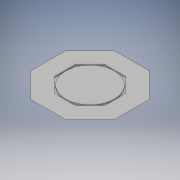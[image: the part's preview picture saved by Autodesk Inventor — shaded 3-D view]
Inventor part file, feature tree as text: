
AUTODESK INVENTOR PART (.ipt)
format: ipt  version: 2016 SP2 (Build 200236200, 236)  size: 265,216 bytes
history: native  units: mm
features: sketch x5, extrude x3, sweep x1, projected_geometry x1
ambient origin geometry x8: Origin, YZ Plane, XZ Plane, XY Plane, X Axis, Y Axis, Z Axis, Center Point
bodies: Body1 (feature_tree)
feature tree (10):
  sweep  "Sweeping2"
  extrude  "Extrusion1"  Depth=8.75mm
  extrude  "Extrusion2"  Depth=7.25mm
  extrude  "Extrusion3"  TaperAngle=0.0deg  [1 undecoded]
  sketch  "Skizze1"  dims[d4=10.5mm d10=50.0mm]
  sketch  "Skizze3"  dims[d11=100.0mm d12=8.75mm]
  sketch  "Skizze4"  dims[d13=8.75mm d14=7.25mm]
  projected_geometry  "Projizierte Kontur1"
  sketch  "Skizze5"  dims[d16=0.0mm d19=0.0mm d20=0.0mm]
  sketch  "Skizze7"  dims[d21=8.75mm d22=100.0mm d23=15.5mm d24=0.0mm d25=5.0mm d26=0.0mm d27=14.0mm d28=11.0mm d29=14.0mm d30=11.0mm d31=6.0mm d32=50.0mm d34=360.0deg d36=14.0mm d37=11.0mm d38=5.0mm d39=120.0mm d41=360.0deg d43=3.0mm d44=0.0mm]
note: 1 required parameter value undecoded (feature->parameter linkage not recoverable at this tier; creation-order binding heuristic only, values carry confidence <= 0.55)
